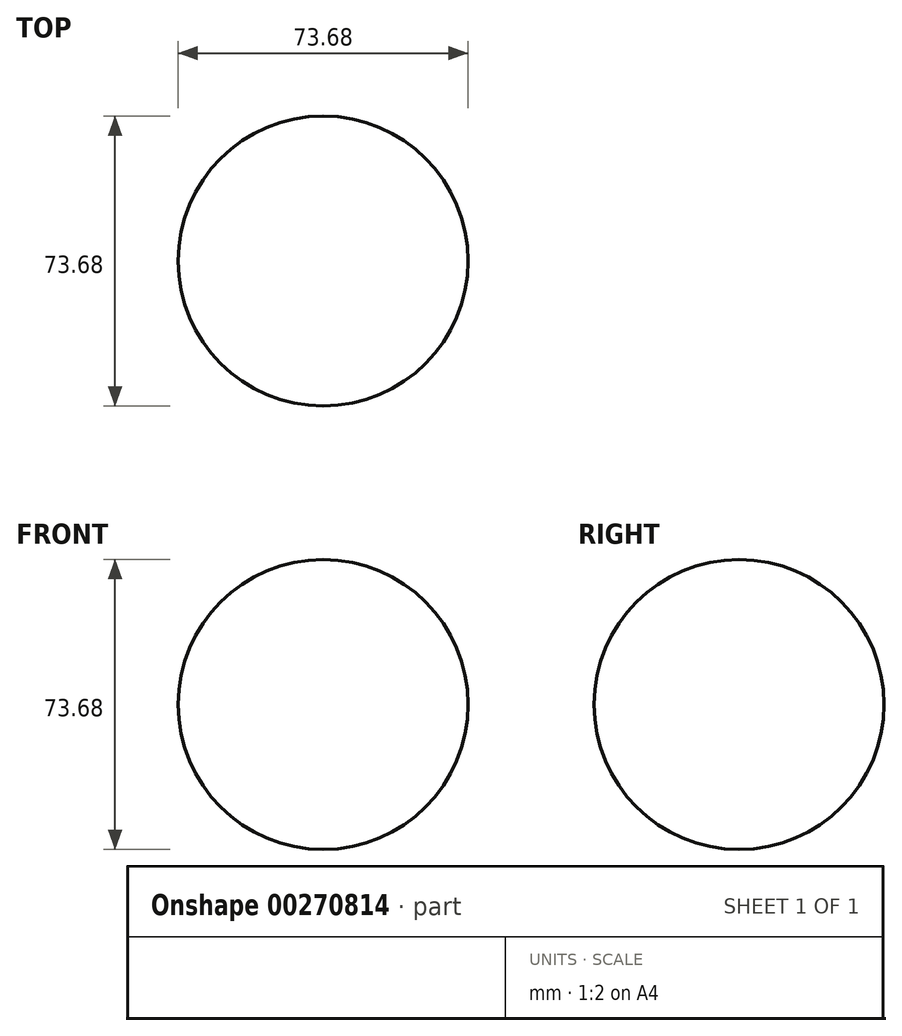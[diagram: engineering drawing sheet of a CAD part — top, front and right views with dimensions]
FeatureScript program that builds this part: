
annotation { "Feature Type Name" : "Feature", "Feature Type Description" : "" }
export const myFeature = defineFeature(function(context is Context, id is Id, definition is map)
    precondition{}
    {
        {
            var Q0;
            Q0=qCreatedBy(makeId("Front.planeOp"),FACE);
            var sketch = newSketch(context, id + "F0", { "sketchPlane" : qUnion([Q0])});
            skArc(sketch, "E0", {"start": v(0, 36.84) * mm, "mid": v(-36.84, 0) * mm, "end": v(0, -36.84) * mm});
            skLineSegment(sketch, "E1", {"start": v(0, 0) * mm, "end": v(0, -36.84) * mm});
            skLineSegment(sketch, "E2", {"start": v(0, -36.84) * mm, "end": v(0, 36.84) * mm});
            skSolve(sketch);
        }
        {
            var Q0;
            {var subQ0=sQuery(id+"F0.wireOp",EDGE,"E0");Q0=makeQuery(id+"F0.imprint","IMPRINT",FACE,{"disambiguationData":[TD([[makeQuery(id+"F0.imprint","IMPRINT",EDGE,{"derivedFrom":subQ0}),1.0]])]});}
            var Q1;
            Q1=sQuery(id+"F0.wireOp",EDGE,"E2");
            revolve(context, id + "F1", {"entities" : qUnion([Q0]), "axis" : qUnion([Q1]), "revolveType" : RevolveType.FULL});
        }
    });
